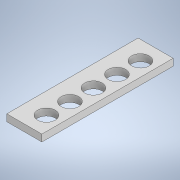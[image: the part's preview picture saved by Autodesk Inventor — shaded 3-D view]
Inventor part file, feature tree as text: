
AUTODESK INVENTOR PART (.ipt)
format: ipt  version: 2020 (Build 240168000, 168)  size: 114,176 bytes
history: native  units: mm
features: extrude x1, sketch x1
ambient origin geometry x8: Origin, YZ Plane, XZ Plane, XY Plane, X Axis, Y Axis, Z Axis, Center Point
bodies: Solide1 (feature_tree)
feature tree (2):
  extrude  "Extrusion1"  Depth=112.0mm
  sketch  "Esquisse1"
